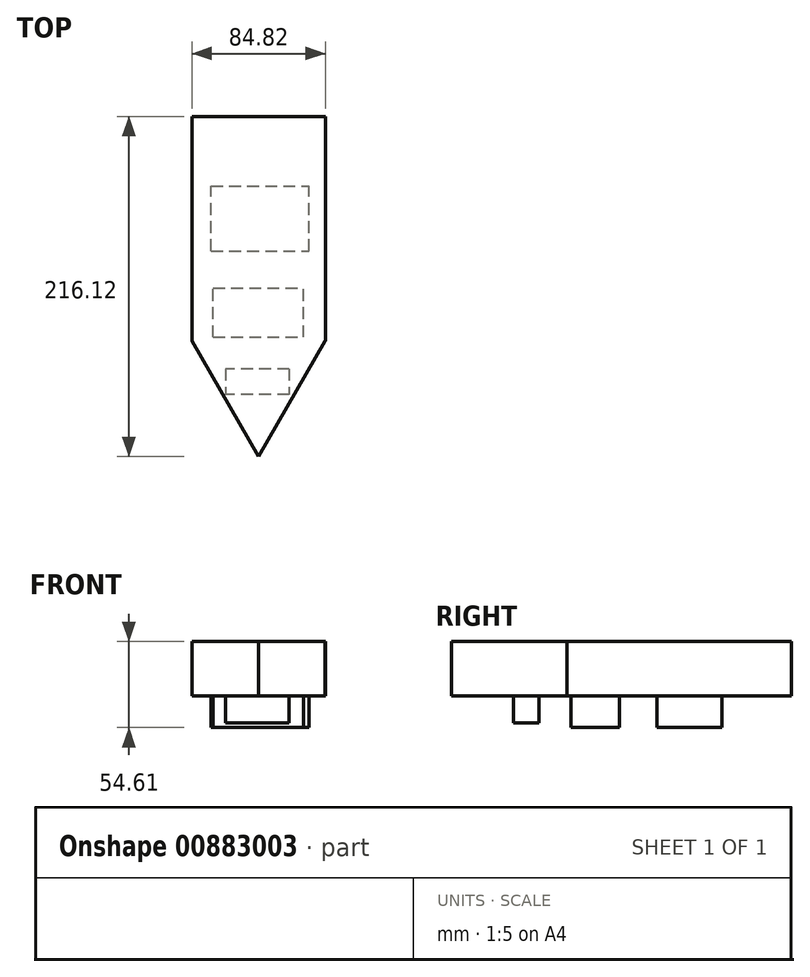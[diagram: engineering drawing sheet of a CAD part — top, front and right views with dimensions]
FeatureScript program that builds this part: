
annotation { "Feature Type Name" : "Feature", "Feature Type Description" : "" }
export const myFeature = defineFeature(function(context is Context, id is Id, definition is map)
    precondition{}
    {
        {
            var Q0;
            Q0=qCreatedBy(makeId("Top.planeOp"),FACE);
            var sketch = newSketch(context, id + "F0", { "sketchPlane" : qUnion([Q0])});
            skPoint(sketch, "E0.0.midPoint", {"position": v(5.61, -65.48) * mm});
            skPoint(sketch, "E1.orphan", {"position": v(-11.22, -43.03) * mm});
            skPoint(sketch, "E0.cCircle.center.orphan", {"position": v(0, -58) * mm});
            skPoint(sketch, "E0.2.end.orphan", {"position": v(18.57, -55.76) * mm});
            skPoint(sketch, "E0.0.end.orphan", {"position": v(-7.35, -75.2) * mm});
            skPoint(sketch, "E2.0.midPoint", {"position": v(8.78, -58) * mm});
            skPoint(sketch, "E3.orphan", {"position": v(8.78, -101.05) * mm});
            skPoint(sketch, "E2.5.end.orphan", {"position": v(8.78, -14.93) * mm});
            skCircle(sketch, "E4.cCircle", {"center": v(0, -58) * mm, "radius": 24.46 * mm, "construction": true});
            skLineSegment(sketch, "E4.0", {"start": v(-42.37, -33.53) * mm, "end": v(42.37, -33.53) * mm});
            skLineSegment(sketch, "E4.1", {"start": v(42.37, -33.53) * mm, "end": v(0, -106.92) * mm});
            skLineSegment(sketch, "E4.2", {"start": v(0, -106.92) * mm, "end": v(-42.37, -33.53) * mm});
            skPoint(sketch, "E4.0.midPoint", {"position": v(0, -33.53) * mm});
            skLineSegment(sketch, "E5.bottom", {"start": v(-42.37, -33.53) * mm, "end": v(42.45, -33.53) * mm});
            skLineSegment(sketch, "E5.left", {"start": v(-42.37, -33.53) * mm, "end": v(-42.37, 77.85) * mm});
            skLineSegment(sketch, "E5.right", {"start": v(42.45, -33.53) * mm, "end": v(42.45, 77.85) * mm});
            skLineSegment(sketch, "E6.left", {"start": v(-6.19, 77.85) * mm, "end": v(-6.19, 77.85) * mm});
            skLineSegment(sketch, "E6.right", {"start": v(0, 77.85) * mm, "end": v(0, 77.85) * mm});
            skLineSegment(sketch, "E7.top", {"start": v(-42.37, 109.2) * mm, "end": v(42.45, 109.2) * mm});
            skLineSegment(sketch, "E7.left", {"start": v(-42.37, 77.85) * mm, "end": v(-42.37, 109.2) * mm});
            skLineSegment(sketch, "E7.right", {"start": v(42.45, 77.85) * mm, "end": v(42.45, 109.2) * mm});
            skSolve(sketch);
        }
        {
            var Q0;
            {var subQ1=sQuery(id+"F0.wireOp",EDGE,"E5.left");Q0=makeQuery(id+"F0.imprint","IMPRINT",FACE,{"disambiguationData":[TD([[makeQuery(id+"F0.imprint","IMPRINT",EDGE,{"derivedFrom":subQ1}),-1.0]])]});}
            var Q1;
            {var subQ0=sQuery(id+"F0.wireOp",EDGE,"E4.1");Q1=makeQuery(id+"F0.imprint","IMPRINT",FACE,{"disambiguationData":[TD([[makeQuery(id+"F0.imprint","IMPRINT",EDGE,{"derivedFrom":subQ0}),-1.0]])]});}
            extrude(context, id + "F1", {"entities" : qUnion([Q0, Q1]), "depth" : 34.54 * mm, "offsetDistance" : 25.4 * mm});
        }
        {
            var Q0;
            Q0=qCreatedBy(makeId("Top.planeOp"),FACE);
            var sketch = newSketch(context, id + "F2", { "sketchPlane" : qUnion([Q0])});
            skLineSegment(sketch, "E8.bottom", {"start": v(19.43, -51.17) * mm, "end": v(-20.87, -51.17) * mm});
            skLineSegment(sketch, "E8.top", {"start": v(19.43, -67.45) * mm, "end": v(-20.87, -67.45) * mm});
            skLineSegment(sketch, "E8.left", {"start": v(19.43, -51.17) * mm, "end": v(19.43, -67.45) * mm});
            skLineSegment(sketch, "E8.right", {"start": v(-20.87, -51.17) * mm, "end": v(-20.87, -67.45) * mm});
            skLineSegment(sketch, "E9", {"start": v(11.08, -33.26) * mm, "end": v(11.08, -31.63) * mm});
            skLineSegment(sketch, "E10", {"start": v(-20.87, -31.63) * mm, "end": v(-15.97, -31.63) * mm});
            skPoint(sketch, "E11.end.orphan", {"position": v(-15.97, -67.45) * mm});
            skSolve(sketch);
        }
        {
            var Q0;
            Q0=makeQuery(id+"F2.imprint","IMPRINT",FACE,{"disambiguationData":[TD([[makeQuery(id+"F2.imprint","IMPRINT",EDGE,{"derivedFrom":sQuery(id+"F2.wireOp",EDGE,"E8.bottom")}),1.0]])]});
            extrude(context, id + "F3", {"entities" : qUnion([Q0]), "operationType" : NewBodyOperationType.ADD, "oppositeDirection" : true, "depth" : 17.27 * mm, "offsetDistance" : 25.4 * mm});
        }
        {
            var Q0;
            Q0=qCreatedBy(makeId("Top.planeOp"),FACE);
            var sketch = newSketch(context, id + "F4", { "sketchPlane" : qUnion([Q0])});
            skLineSegment(sketch, "E12.bottom", {"start": v(-28.85, -31.05) * mm, "end": v(28.52, -31.05) * mm});
            skLineSegment(sketch, "E12.top", {"start": v(-28.85, 0) * mm, "end": v(28.52, 0) * mm});
            skLineSegment(sketch, "E12.left", {"start": v(-28.85, -31.05) * mm, "end": v(-28.85, 0) * mm});
            skLineSegment(sketch, "E12.right", {"start": v(28.52, -31.05) * mm, "end": v(28.52, 0) * mm});
            skLineSegment(sketch, "E13.bottom", {"start": v(-30.18, 23.65) * mm, "end": v(32.19, 23.65) * mm});
            skLineSegment(sketch, "E13.top", {"start": v(-30.18, 65.01) * mm, "end": v(32.19, 65.01) * mm});
            skLineSegment(sketch, "E13.left", {"start": v(-30.18, 23.65) * mm, "end": v(-30.18, 65.01) * mm});
            skLineSegment(sketch, "E13.right", {"start": v(32.19, 23.65) * mm, "end": v(32.19, 65.01) * mm});
            skSolve(sketch);
        }
        {
            var Q0;
            Q0=makeQuery(id+"F4.imprint","IMPRINT",FACE,{"disambiguationData":[TD([[makeQuery(id+"F4.imprint","IMPRINT",EDGE,{"derivedFrom":sQuery(id+"F4.wireOp",EDGE,"E13.bottom")}),1.0]])]});
            var Q1;
            Q1=makeQuery(id+"F4.imprint","IMPRINT",FACE,{"disambiguationData":[TD([[makeQuery(id+"F4.imprint","IMPRINT",EDGE,{"derivedFrom":sQuery(id+"F4.wireOp",EDGE,"E12.bottom")}),1.0]])]});
            extrude(context, id + "F5", {"entities" : qUnion([Q0, Q1]), "operationType" : NewBodyOperationType.ADD, "oppositeDirection" : true, "depth" : 20.07 * mm, "offsetDistance" : 25.4 * mm});
        }
    });
